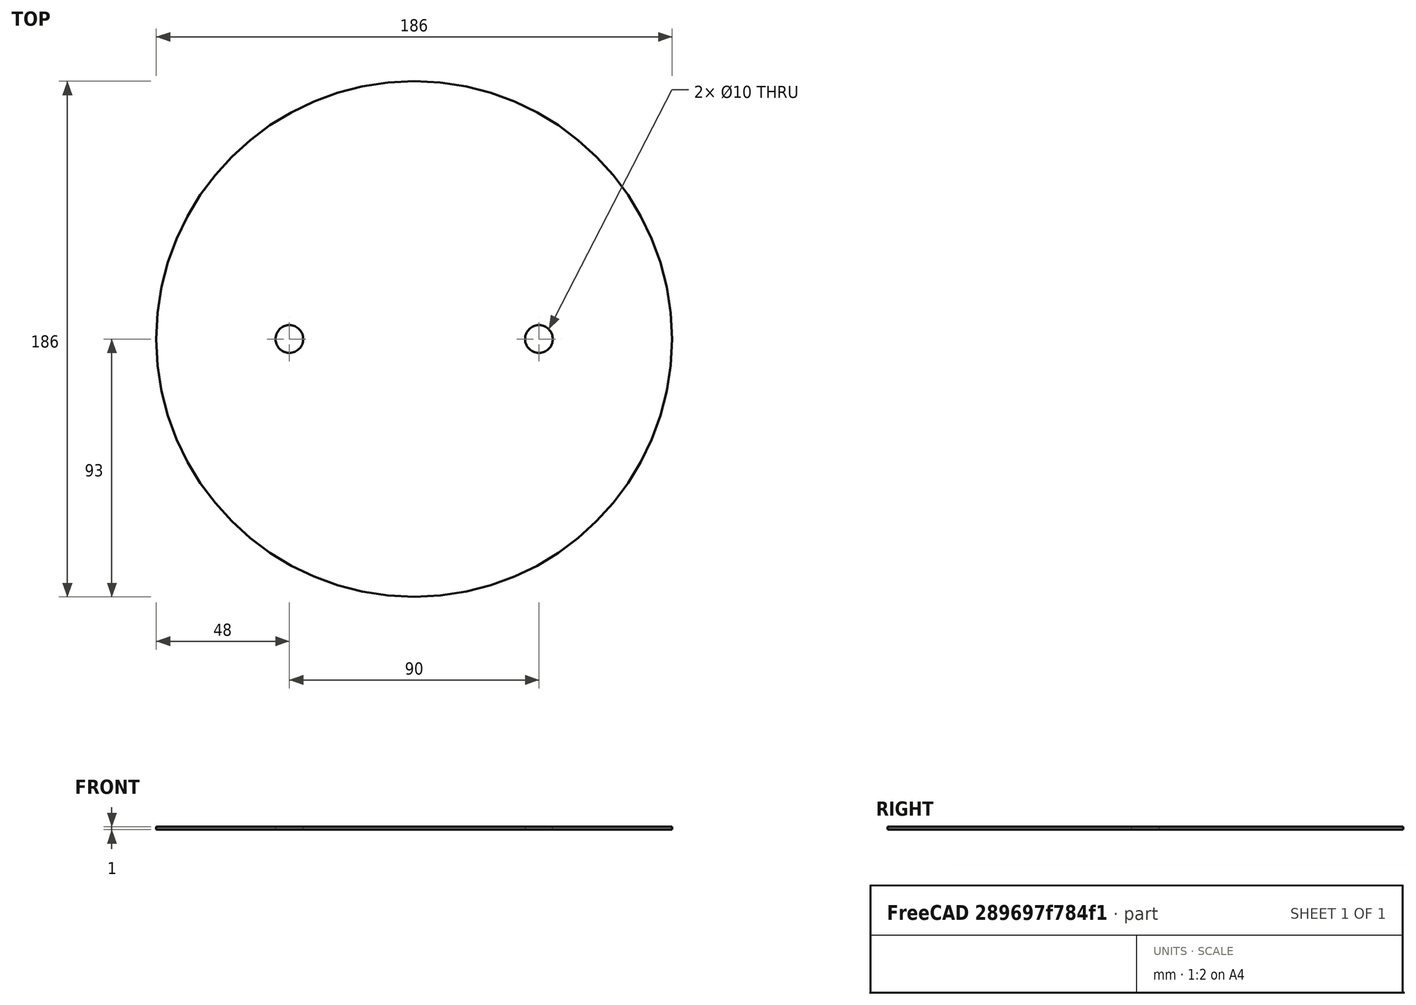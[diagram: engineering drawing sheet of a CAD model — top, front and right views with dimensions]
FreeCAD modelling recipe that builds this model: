
FCSTD DOCUMENT  (FreeCAD 0.19R24276 (Git))
Label: MS_v3
License: All rights reserved
LicenseURL: http://en.wikipedia.org/wiki/All_rights_reserved
objects: Sketcher::SketchObject×1, PartDesign::Pad×1, PartDesign::Body×1
note: 4 computed .brp shape members not serialized (recipe doc carries the construction recipe); baked Part::Feature solids carry a one-line shape summary decoded from their .brp

FEATURE [Sketcher::SketchObject] Sketch
  FullyConstrained = false
  MapMode = 5
  Support = -> [XY_Plane]
  sketch-geometry (3):
    g0: Circle CenterX=-45 CenterY=0 CenterZ=0 NormalX=0 NormalY=0 NormalZ=1 AngleXU=0 Radius=5
    g1: Circle CenterX=45 CenterY=0 CenterZ=0 NormalX=0 NormalY=0 NormalZ=1 AngleXU=0 Radius=5
    g2: Circle CenterX=0 CenterY=0 CenterZ=0 NormalX=0 NormalY=0 NormalZ=1 AngleXU=0 Radius=93
  constraints (6):
    c: PointOnObject(g0,g-1)
    c: PointOnObject(g1,g-1)
    c: Diameter(g0) = 10
    c: Equal(g0,g1)
    c: Coincident(g2,g-1)
    c: Diameter(g2) = 186
FEATURE [PartDesign::Pad] Pad
  Direction = (1,1,1)
  Length = 1
  Length2 = 100
  Profile = -> Sketch
  Type = 0
FEATURE [PartDesign::Body] Body
  Group = -> [Sketch,Pad]
  Origin = -> Origin
  Tip = -> Pad
